FCSTD DOCUMENT  (FreeCAD 1.0R39109 (Git))
Label: 70_drawer_box_assembly
License: All rights reserved
LicenseURL: http://en.wikipedia.org/wiki/All_rights_reserved
objects: App::FeaturePython×25, App::Link×9, TechDraw::DrawViewDimension×7, TechDraw::DrawProjGroupItem×5, Assembly::JointGroup×2, Assembly::AssemblyObject×2, TechDraw::DrawSVGTemplate×1, TechDraw::DrawProjGroup×1, TechDraw::DrawPage×1
note: 13 computed .brp shape members not serialized (recipe doc carries the construction recipe); baked Part::Feature solids carry a one-line shape summary decoded from their .brp
EXTERNAL_REF file=71_drawer_box_top_bottom.FCStd obj=Body
EXTERNAL_REF file=73_drawer_box_side_b.FCStd obj=Body
EXTERNAL_REF file=72_drawer_box_side_a.FCStd obj=Body
EXTERNAL_REF file=junker_kv1-45-h45-l300-sc/kv1_h45_l350.FCStd obj=KV1_45_H45_L____SC
EXTERNAL_REF file=75_drawer_box_stabilizer.FCStd obj=Body

FEATURE [App::Link] Body
  LinkPlacement = pos=(0,0,0) rot=(0,0,1;3.14159rad)
  LinkedObject = -> <external 71_drawer_box_top_bottom.FCStd>#Body
  Placement = pos=(0,0,0) rot=(0,0,1;3.14159rad)
FEATURE [App::FeaturePython] GroundedJoint  # Assembly grounded joint (typed FeaturePython)
  ObjectToGround = -> Body
  Placement = pos=(0,0,0) rot=(0,0,1;3.14159rad)
FEATURE [App::Link] Body003
  LinkPlacement = pos=(2.045e-13,-6.16e-14,-771) rot=(1,0,0;3.14159rad)
  LinkedObject = -> <external 71_drawer_box_top_bottom.FCStd>#Body
  Placement = pos=(2.045e-13,-6.16e-14,-771) rot=(1,0,0;3.14159rad)
FEATURE [App::Link] Body004
  LinkPlacement = pos=(-262.5,7.5,-385.5) rot=(0,1,0;1.5708rad)
  LinkedObject = -> <external 73_drawer_box_side_b.FCStd>#Body
  Placement = pos=(-262.5,7.5,-385.5) rot=(0,1,0;1.5708rad)
FEATURE [App::Link] Body005
  LinkPlacement = pos=(244.5,7.5,-385.5) rot=(0,1,0;1.5708rad)
  LinkedObject = -> <external 72_drawer_box_side_a.FCStd>#Body
  Placement = pos=(244.5,7.5,-385.5) rot=(0,1,0;1.5708rad)
FEATURE [App::Link] KV1_45_H45_L____SC  label="KV1-45-H45-L...-SC"
  LinkPlacement = pos=(238.45,-31,-32) rot=(0,0.707107,-0.707107;3.14159rad)
  LinkedObject = -> <external junker_kv1-45-h45-l300-sc/kv1_h45_l350.FCStd>#KV1_45_H45_L____SC
  Placement = pos=(238.45,-31,-32) rot=(0,0.707107,-0.707107;3.14159rad)
FEATURE [TechDraw::DrawSVGTemplate] Template
  Height = 210
  Orientation = 1
  Template = C:/Program Files/FreeCAD 1.0/data/Mod/TechDraw/Templates/Default_Template_A4_Landscape.svg
  Width = 297
FEATURE [TechDraw::DrawProjGroupItem] View  label="Front"
  CoarseView = false
  Direction = (0,-1,0)
  Focus = 100
  HardHidden = false
  IsoCount = 0
  IsoHidden = false
  IsoVisible = false
  LockPosition = true
  Perspective = false
  Rotation = 0
  RotationVector = (1,0,0)
  Scale = 0.1
  ScaleType = 2
  ScrubCount = 1
  SeamHidden = false
  SeamVisible = true
  SmoothHidden = false
  SmoothVisible = true
  Type = 0
  X = 0
  XDirection = (1,0,0)
  XSource = -> [Body,Body003,Body004,Body005,KV1_45_H45_L____SC,Body007]
  Y = 0
FEATURE [TechDraw::DrawProjGroupItem] ProjItem  label="Right"
  CoarseView = false
  Direction = (1,-1e-16,0)
  Focus = 100
  HardHidden = false
  IsoCount = 0
  IsoHidden = false
  IsoVisible = false
  LockPosition = false
  Perspective = false
  Rotation = 0
  RotationVector = (1,0,0)
  ScaleType = 0
  ScrubCount = 1
  SeamHidden = false
  SeamVisible = true
  SmoothHidden = false
  SmoothVisible = true
  Type = 2
  X = -60.9
  XDirection = (1e-16,1,0)
  XSource = -> [Body,Body003,Body004,Body005,KV1_45_H45_L____SC,Body007]
  Y = 0
FEATURE [TechDraw::DrawProjGroupItem] ProjItem001  label="Bottom"
  CoarseView = false
  Direction = (0,0,-1)
  Focus = 100
  HardHidden = false
  IsoCount = 0
  IsoHidden = false
  IsoVisible = false
  LockPosition = false
  Perspective = false
  Rotation = 0
  RotationVector = (1,0,0)
  ScaleType = 0
  ScrubCount = 1
  SeamHidden = false
  SeamVisible = true
  SmoothHidden = false
  SmoothVisible = true
  Type = 5
  X = 0
  XDirection = (1,0,0)
  XSource = -> [Body,Body003,Body004,Body005,KV1_45_H45_L____SC,Body007]
  Y = 75
FEATURE [TechDraw::DrawProjGroupItem] ProjItem002  label="Left"
  CoarseView = false
  Direction = (-1,-1e-16,0)
  Focus = 100
  HardHidden = false
  IsoCount = 0
  IsoHidden = false
  IsoVisible = false
  LockPosition = false
  Perspective = false
  Rotation = 0
  RotationVector = (1,0,0)
  ScaleType = 0
  ScrubCount = 1
  SeamHidden = false
  SeamVisible = true
  SmoothHidden = false
  SmoothVisible = true
  Type = 1
  X = 60.9
  XDirection = (1e-16,-1,0)
  XSource = -> [Body,Body003,Body004,Body005,KV1_45_H45_L____SC,Body007]
  Y = 0
FEATURE [TechDraw::DrawProjGroupItem] ProjItem003  label="Top"
  CoarseView = false
  Direction = (0,0,1)
  Focus = 100
  HardHidden = false
  IsoCount = 0
  IsoHidden = false
  IsoVisible = false
  LockPosition = false
  Perspective = false
  Rotation = 0
  RotationVector = (1,0,0)
  ScaleType = 0
  ScrubCount = 1
  SeamHidden = false
  SeamVisible = true
  SmoothHidden = false
  SmoothVisible = true
  Type = 4
  X = 0
  XDirection = (1,0,0)
  XSource = -> [Body,Body003,Body004,Body005,KV1_45_H45_L____SC,Body007]
  Y = -75
FEATURE [TechDraw::DrawProjGroup] ProjGroup
  Anchor = -> View
  AutoDistribute = true
  LockPosition = false
  ProjectionType = 0
  Rotation = 0
  Scale = 0.1
  ScaleType = 2
  Views = -> [View,ProjItem,ProjItem001,ProjItem002,ProjItem003]
  X = 148.5
  XSource = -> [Body,Body003,Body004,Body005,KV1_45_H45_L____SC,Body007]
  Y = 105
  spacingX = 15
  spacingY = 15
FEATURE [TechDraw::DrawViewDimension] Dimension
  AngleOverride = false
  Arbitrary = false
  ArbitraryTolerances = false
  BoxCorners = (2) [(-26.25,-40.35,0),(26.25,40.35,0)]
  EqualTolerance = true
  ExtensionAngle = 0
  FormatSpec = %.2w
  FormatSpecOverTolerance = %+.2w
  FormatSpecUnderTolerance = %+.2w
  Inverted = false
  LineAngle = 0
  LockPosition = false
  MeasureType = 1
  OverTolerance = 0
  References2D = -> [View]
  Rotation = 0
  ScaleType = 0
  TheoreticalExact = false
  Type = 0
  UnderTolerance = 0
  X = 32.776
  Y = -39.775
FEATURE [TechDraw::DrawViewDimension] Dimension001
  AngleOverride = false
  Arbitrary = false
  ArbitraryTolerances = false
  BoxCorners = (2) [(-26.25,-40.35,0),(26.25,40.35,0)]
  EqualTolerance = true
  ExtensionAngle = 0
  FormatSpec = %.2w
  FormatSpecOverTolerance = %+.2w
  FormatSpecUnderTolerance = %+.2w
  Inverted = false
  LineAngle = 0
  LockPosition = false
  MeasureType = 1
  OverTolerance = 0
  References2D = -> [View]
  Rotation = 0
  ScaleType = 0
  TheoreticalExact = false
  Type = 0
  UnderTolerance = 0
  X = 32.776
  Y = 35.9189
FEATURE [TechDraw::DrawViewDimension] Dimension002
  AngleOverride = false
  Arbitrary = false
  ArbitraryTolerances = false
  BoxCorners = (2) [(-26.25,-40.35,0),(26.25,40.35,0)]
  EqualTolerance = true
  ExtensionAngle = 0
  FormatSpec = %.2w
  FormatSpecOverTolerance = %+.2w
  FormatSpecUnderTolerance = %+.2w
  Inverted = false
  LineAngle = 0
  LockPosition = false
  MeasureType = 1
  OverTolerance = 0
  References2D = -> [View]
  Rotation = 0
  ScaleType = 0
  TheoreticalExact = false
  Type = 0
  UnderTolerance = 0
  X = 36.8541
  Y = 21.3236
FEATURE [App::Link] Body007
  LinkPlacement = pos=(-2.61e-14,196.5,-386) rot=(0,-0.707107,0.707107;3.14159rad)
  LinkedObject = -> <external 75_drawer_box_stabilizer.FCStd>#Body
  Placement = pos=(-2.61e-14,196.5,-386) rot=(0,-0.707107,0.707107;3.14159rad)
FEATURE [App::FeaturePython] Joint  label="Distance"  # Assembly joint (typed FeaturePython)
  Activated = true
  AngleMax = 0
  AngleMin = 0
  Detach1 = false
  Detach2 = false
  Distance = 0
  Distance2 = 0
  EnableAngleMax = false
  EnableAngleMin = false
  EnableLengthMax = false
  EnableLengthMin = false
  JointType = 5 (Distance)
  LengthMax = 0
  LengthMin = 0
  Placement1 = pos=(-385.5,-1.21012,9.03703) rot=(-0.57735,-0.57735,0.57735;2.0944rad)
  Placement2 = pos=(5.5e-15,3.01501,0) rot=(0,0,1;0rad)
  Reference1 = -> Assembly [Body005.Face2,Body005.Vertex7]
  Reference2 = -> Assembly [Body.Face4,Body.Vertex10]
FEATURE [App::FeaturePython] Joint001  label="Distance001"  # Assembly joint (typed FeaturePython)
  Activated = true
  AngleMax = 0
  AngleMin = 0
  Detach1 = false
  Detach2 = false
  Distance = 0
  Distance2 = 0
  EnableAngleMax = false
  EnableAngleMin = false
  EnableLengthMax = false
  EnableLengthMin = false
  JointType = 5 (Distance)
  LengthMax = 0
  LengthMin = 0
  Placement1 = pos=(0,189,9) rot=(-1,0,0;1.5708rad)
  Placement2 = pos=(-5.9e-15,-196.5,9) rot=(0,0.707107,-0.707107;3.14159rad)
  Reference1 = -> Assembly [Body005.Face1,Body005.Vertex2]
  Reference2 = -> Assembly [Body.Face6,Body.Vertex6]
FEATURE [App::FeaturePython] Joint002  label="Distance002"  # Assembly joint (typed FeaturePython)
  Activated = true
  AngleMax = 0
  AngleMin = 0
  Detach1 = false
  Detach2 = false
  Distance = 0
  Distance2 = 0
  EnableAngleMax = false
  EnableAngleMin = false
  EnableLengthMax = false
  EnableLengthMin = false
  JointType = 5 (Distance)
  LengthMax = 0
  LengthMin = 0
  Placement1 = pos=(-262.5,-4.6e-15,9) rot=(-0.57735,-0.57735,0.57735;2.0944rad)
  Placement2 = pos=(0,3.6e-15,18) rot=(0,0,1;0rad)
  Reference1 = -> Assembly [Body.Face2,Body.Vertex6]
  Reference2 = -> Assembly [Body005.Face5,Body005.Vertex2]
FEATURE [App::FeaturePython] Joint003  label="Distance003"  # Assembly joint (typed FeaturePython)
  Activated = true
  AngleMax = 0
  AngleMin = 0
  Detach1 = false
  Detach2 = false
  Distance = 0
  Distance2 = 0
  EnableAngleMax = false
  EnableAngleMin = false
  EnableLengthMax = false
  EnableLengthMin = false
  JointType = 5 (Distance)
  LengthMax = 0
  LengthMin = 0
  Placement1 = pos=(-385.5,-1.21012,8.96297) rot=(-0.57735,-0.57735,0.57735;2.0944rad)
  Placement2 = pos=(5.5e-15,3.01501,0) rot=(0,0,1;0rad)
  Reference1 = -> Assembly [Body004.Face2,Body004.Face2]
  Reference2 = -> Assembly [Body.Face4,Body.Vertex3]
FEATURE [App::FeaturePython] Joint004  label="Distance004"  # Assembly joint (typed FeaturePython)
  Activated = true
  AngleMax = 0
  AngleMin = 0
  Detach1 = false
  Detach2 = false
  Distance = 0
  Distance2 = 0
  EnableAngleMax = false
  EnableAngleMin = false
  EnableLengthMax = false
  EnableLengthMin = false
  JointType = 5 (Distance)
  LengthMax = 0
  LengthMin = 0
  Placement1 = pos=(-5.9e-15,-196.5,9) rot=(0,0.707107,-0.707107;3.14159rad)
  Placement2 = pos=(0,189,9) rot=(-1,0,0;1.5708rad)
  Reference1 = -> Assembly [Body.Face6,Body.Vertex7]
  Reference2 = -> Assembly [Body004.Face1,Body004.Vertex1]
FEATURE [App::FeaturePython] Joint005  label="Distance005"  # Assembly joint (typed FeaturePython)
  Activated = true
  AngleMax = 0
  AngleMin = 0
  Detach1 = false
  Detach2 = false
  Distance = 0
  Distance2 = 0
  EnableAngleMax = false
  EnableAngleMin = false
  EnableLengthMax = false
  EnableLengthMin = false
  JointType = 5 (Distance)
  LengthMax = 0
  LengthMin = 0
  Placement1 = pos=(262.5,4.6e-15,9) rot=(-0.57735,0.57735,-0.57735;2.0944rad)
  Placement2 = pos=(0,7.1e-15,0) rot=(0,0,1;0rad)
  Reference1 = -> Assembly [Body.Face3,Body.Vertex8]
  Reference2 = -> Assembly [Body004.Face4,Body004.Vertex1]
FEATURE [App::FeaturePython] Joint006  label="Distance006"  # Assembly joint (typed FeaturePython)
  Activated = true
  AngleMax = 0
  AngleMin = 0
  Detach1 = false
  Detach2 = false
  Distance = 0
  Distance2 = 0
  EnableAngleMax = false
  EnableAngleMin = false
  EnableLengthMax = false
  EnableLengthMin = false
  JointType = 5 (Distance)
  LengthMax = 0
  LengthMin = 0
  Placement1 = pos=(-262.5,-6.4e-15,9) rot=(-0.57735,-0.57735,0.57735;2.0944rad)
  Placement2 = pos=(0,7.1e-15,0) rot=(0,0,1;0rad)
  Reference1 = -> Assembly [Body003.Face2,Body003.Vertex1]
  Reference2 = -> Assembly [Body004.Face4,Body004.Vertex3]
FEATURE [App::FeaturePython] Joint007  label="Distance007"  # Assembly joint (typed FeaturePython)
  Activated = true
  AngleMax = 0
  AngleMin = 0
  Detach1 = false
  Detach2 = false
  Distance = 0
  Distance2 = 0
  EnableAngleMax = false
  EnableAngleMin = false
  EnableLengthMax = false
  EnableLengthMin = false
  JointType = 5 (Distance)
  LengthMax = 0
  LengthMin = 0
  Placement1 = pos=(4.7e-15,3.01501,0) rot=(0,0,1;0rad)
  Placement2 = pos=(385.5,-1.21012,8.96297) rot=(-0.57735,0.57735,-0.57735;2.0944rad)
  Reference1 = -> Assembly [Body003.Face4,Body003.Vertex1]
  Reference2 = -> Assembly [Body004.Face3,Body004.Vertex13]
FEATURE [App::FeaturePython] Joint008  label="Distance008"  # Assembly joint (typed FeaturePython)
  Activated = true
  AngleMax = 0
  AngleMin = 0
  Detach1 = false
  Detach2 = false
  Distance = 0
  Distance2 = 0
  EnableAngleMax = false
  EnableAngleMin = false
  EnableLengthMax = false
  EnableLengthMin = false
  JointType = 5 (Distance)
  LengthMax = 0
  LengthMin = 0
  Placement1 = pos=(-2e-16,-196.5,9) rot=(0,0.707107,-0.707107;3.14159rad)
  Placement2 = pos=(0,189,9) rot=(-1,0,0;1.5708rad)
  Reference1 = -> Assembly [Body003.Face6,Body003.Vertex5]
  Reference2 = -> Assembly [Body004.Face1,Body004.Vertex4]
FEATURE [App::FeaturePython] Joint009  label="Distance009"  # Assembly joint (typed FeaturePython)
  Activated = true
  AngleMax = 0
  AngleMin = 0
  Detach1 = false
  Detach2 = false
  Distance = 0
  Distance2 = 0
  EnableAngleMax = false
  EnableAngleMin = false
  EnableLengthMax = false
  EnableLengthMin = false
  JointType = 5 (Distance)
  LengthMax = 0
  LengthMin = 0
  Placement1 = pos=(-244.5,7.39e-13,8.98683) rot=(0.57735,0.57735,-0.57735;4.18879rad)
  Placement2 = pos=(0.0538161,-6.11853,0) rot=(0,0,1;0rad)
  Reference1 = -> Assembly [Body007.Face5,Body007.Face5]
  Reference2 = -> Assembly [Body005.Face6,Body005.Vertex47]
FEATURE [App::FeaturePython] Joint010  label="Distance010"  # Assembly joint (typed FeaturePython)
  Activated = true
  AngleMax = 0
  AngleMin = 0
  Detach1 = false
  Detach2 = false
  Distance = 0
  Distance2 = 0
  EnableAngleMax = false
  EnableAngleMin = false
  EnableLengthMax = false
  EnableLengthMin = false
  JointType = 5 (Distance)
  LengthMax = 0
  LengthMin = 0
  Placement1 = pos=(-1.29e-14,0,0) rot=(0,0,1;0rad)
  Placement2 = pos=(0,189,9) rot=(-1,0,0;1.5708rad)
  Reference1 = -> Assembly [Body007.Face2,Body007.Face2]
  Reference2 = -> Assembly [Body004.Face1,Body004.Face1]
FEATURE [App::FeaturePython] Joint011  label="Distance011"  # Assembly joint (typed FeaturePython)
  Activated = true
  AngleMax = 0
  AngleMin = 0
  Detach1 = false
  Detach2 = false
  Distance = 335.5
  Distance2 = 0
  EnableAngleMax = false
  EnableAngleMin = false
  EnableLengthMax = false
  EnableLengthMin = false
  JointType = 5 (Distance)
  LengthMax = 0
  LengthMin = 0
  Placement1 = pos=(-8.8e-15,-50.5,3) rot=(0,0.707107,-0.707107;3.14159rad)
  Placement2 = pos=(5.5e-15,3.01501,0) rot=(0,0,1;0rad)
  Reference1 = -> Assembly [Body007.Face6,Body007.Face6]
  Reference2 = -> Assembly [Body.Face4,Body.Vertex10]
  expr: Distance = (771 - 100) / 2
FEATURE [App::FeaturePython] Joint012  label="Distance012"  # Assembly joint (typed FeaturePython)
  Activated = true
  AngleMax = 0
  AngleMin = 0
  Detach1 = false
  Detach2 = false
  Distance = 0
  Distance2 = 0
  EnableAngleMax = false
  EnableAngleMin = false
  EnableLengthMax = false
  EnableLengthMin = false
  JointType = 5 (Distance)
  LengthMax = 0
  LengthMin = 0
  Placement1 = pos=(-1.2,0.000268538,-180.383) rot=(-0.57735,-0.57735,0.57735;2.0944rad)
  Placement2 = pos=(0.0538161,-6.11853,0) rot=(0,0,1;0rad)
  Reference1 = -> Assembly [KV1_45_H45_L____SC.Junker_H45SC_op_350.Part__Feature.Face126,KV1_45_H45_L____SC.Junker_H45SC_op_350.Part__Feature.Vertex163]
  Reference2 = -> Assembly [Body005.Face6,Body005.Vertex6]
FEATURE [App::FeaturePython] Joint013  label="Distance013"  # Assembly joint (typed FeaturePython)
  Activated = true
  AngleMax = 0
  AngleMin = 0
  Detach1 = false
  Detach2 = false
  Distance = -0.5
  Distance2 = 0
  EnableAngleMax = false
  EnableAngleMin = false
  EnableLengthMax = false
  EnableLengthMin = false
  JointType = 5 (Distance)
  LengthMax = 0
  LengthMin = 0
  Placement1 = pos=(0,-189,9) rot=(0,-0.707107,0.707107;3.14159rad)
  Placement2 = pos=(1.78975,1.17e-14,0) rot=(0,0,1;0rad)
  Reference1 = -> Assembly [Body005.Face10,Body005.Face10]
  Reference2 = -> Assembly [KV1_45_H45_L____SC.Junker_H45SC_op_350.Part__Feature.Face145,KV1_45_H45_L____SC.Junker_H45SC_op_350.Part__Feature.Face145]
FEATURE [App::FeaturePython] Joint014  label="Cylindrical"  # Assembly joint (typed FeaturePython)
  Activated = true
  AngleMax = 0
  AngleMin = 0
  Detach1 = false
  Detach2 = false
  Distance = 0
  Distance2 = 0
  EnableAngleMax = false
  EnableAngleMin = false
  EnableLengthMax = false
  EnableLengthMin = false
  JointType = 2 (Cylindrical)
  LengthMax = 0
  LengthMin = 0
  Placement1 = pos=(-353.5,-81,4.5) rot=(0,0,1;0rad)
  Placement2 = pos=(-0.6,0,-107.5) rot=(0,1,0;1.5708rad)
  Reference1 = -> Assembly [Body005.Face11,Body005.Face11]
  Reference2 = -> Assembly [KV1_45_H45_L____SC.Junker_H45SC_op_350.Part__Feature.Face31,KV1_45_H45_L____SC.Junker_H45SC_op_350.Part__Feature.Face31]
FEATURE [Assembly::JointGroup] Joints001
FEATURE [Assembly::AssemblyObject] Assembly001
  Group = -> [Joints001]
  Origin = -> Origin001
  Type = Assembly
FEATURE [App::Link] KV1_45_H45_L____SC001  label="KV1-45-H45-L...-SC001"
  LinkPlacement = pos=(238.45,-31,-224) rot=(0,0.707107,-0.707107;3.14159rad)
  LinkedObject = -> <external junker_kv1-45-h45-l300-sc/kv1_h45_l350.FCStd>#KV1_45_H45_L____SC
  Placement = pos=(238.45,-31,-224) rot=(0,0.707107,-0.707107;3.14159rad)
FEATURE [App::Link] KV1_45_H45_L____SC002  label="KV1-45-H45-L...-SC002"
  LinkPlacement = pos=(238.45,-31,-128) rot=(0,0.707107,-0.707107;3.14159rad)
  LinkedObject = -> <external junker_kv1-45-h45-l300-sc/kv1_h45_l350.FCStd>#KV1_45_H45_L____SC
  Placement = pos=(238.45,-31,-128) rot=(0,0.707107,-0.707107;3.14159rad)
FEATURE [App::Link] KV1_45_H45_L____SC003  label="KV1-45-H45-L...-SC003"
  LinkPlacement = pos=(238.45,-31,-320) rot=(0,0.707107,-0.707107;3.14159rad)
  LinkedObject = -> <external junker_kv1-45-h45-l300-sc/kv1_h45_l350.FCStd>#KV1_45_H45_L____SC
  Placement = pos=(238.45,-31,-320) rot=(0,0.707107,-0.707107;3.14159rad)
FEATURE [App::FeaturePython] Joint015  label="Distance014"  # Assembly joint (typed FeaturePython)
  Activated = true
  AngleMax = 0
  AngleMin = 0
  Detach1 = false
  Detach2 = false
  Distance = 0
  Distance2 = 0
  EnableAngleMax = false
  EnableAngleMin = false
  EnableLengthMax = false
  EnableLengthMin = false
  JointType = 5 (Distance)
  LengthMax = 0
  LengthMin = 0
  Placement1 = pos=(-1.2,0.000268538,-180.383) rot=(-0.57735,-0.57735,0.57735;2.0944rad)
  Placement2 = pos=(0.0538161,-6.11853,0) rot=(0,0,1;0rad)
  Reference1 = -> Assembly [KV1_45_H45_L____SC002.Junker_H45SC_op_350.Part__Feature.Face126,KV1_45_H45_L____SC002.Junker_H45SC_op_350.Part__Feature.Vertex163]
  Reference2 = -> Assembly [Body005.Face6,Body005.Vertex23]
FEATURE [App::FeaturePython] Joint016  label="Distance015"  # Assembly joint (typed FeaturePython)
  Activated = true
  AngleMax = 0
  AngleMin = 0
  Detach1 = false
  Detach2 = false
  Distance = -0.5
  Distance2 = 0
  EnableAngleMax = false
  EnableAngleMin = false
  EnableLengthMax = false
  EnableLengthMin = false
  JointType = 5 (Distance)
  LengthMax = 0
  LengthMin = 0
  Placement1 = pos=(0,-189,9) rot=(0,-0.707107,0.707107;3.14159rad)
  Placement2 = pos=(1.78975,1.17e-14,0) rot=(0,0,1;0rad)
  Reference1 = -> Assembly [Body005.Face10,Body005.Vertex5]
  Reference2 = -> Assembly [KV1_45_H45_L____SC002.Junker_H45SC_op_350.Part__Feature.Face145,KV1_45_H45_L____SC002.Junker_H45SC_op_350.Part__Feature.Face145]
FEATURE [App::FeaturePython] Joint017  label="Distance016"  # Assembly joint (typed FeaturePython)
  Activated = true
  AngleMax = 0
  AngleMin = 0
  Detach1 = false
  Detach2 = false
  Distance = 0
  Distance2 = 0
  EnableAngleMax = false
  EnableAngleMin = false
  EnableLengthMax = false
  EnableLengthMin = false
  JointType = 5 (Distance)
  LengthMax = 0
  LengthMin = 0
  Placement1 = pos=(-1.2,0.000268538,-180.383) rot=(-0.57735,-0.57735,0.57735;2.0944rad)
  Placement2 = pos=(0.0538161,-6.11853,0) rot=(0,0,1;0rad)
  Reference1 = -> Assembly [KV1_45_H45_L____SC003.Junker_H45SC_op_350.Part__Feature.Face126,KV1_45_H45_L____SC003.Junker_H45SC_op_350.Part__Feature.Vertex171]
  Reference2 = -> Assembly [Body005.Face6,Body005.Vertex21]
FEATURE [App::FeaturePython] Joint018  label="Distance017"  # Assembly joint (typed FeaturePython)
  Activated = true
  AngleMax = 0
  AngleMin = 0
  Detach1 = false
  Detach2 = false
  Distance = 0.5
  Distance2 = 0
  EnableAngleMax = false
  EnableAngleMin = false
  EnableLengthMax = false
  EnableLengthMin = false
  JointType = 5 (Distance)
  LengthMax = 0
  LengthMin = 0
  Placement1 = pos=(1.78975,1.17e-14,0) rot=(0,0,1;0rad)
  Placement2 = pos=(0,-189,9) rot=(0,-0.707107,0.707107;3.14159rad)
  Reference1 = -> Assembly [KV1_45_H45_L____SC003.Junker_H45SC_op_350.Part__Feature.Face145,KV1_45_H45_L____SC003.Junker_H45SC_op_350.Part__Feature.Vertex242]
  Reference2 = -> Assembly [Body005.Face10,Body005.Face10]
FEATURE [App::FeaturePython] Joint019  label="Distance018"  # Assembly joint (typed FeaturePython)
  Activated = true
  AngleMax = 0
  AngleMin = 0
  Detach1 = false
  Detach2 = false
  Distance = 0
  Distance2 = 0
  EnableAngleMax = false
  EnableAngleMin = false
  EnableLengthMax = false
  EnableLengthMin = false
  JointType = 5 (Distance)
  LengthMax = 0
  LengthMin = 0
  Placement1 = pos=(-1.2,0.000268538,-180.383) rot=(-0.57735,-0.57735,0.57735;2.0944rad)
  Placement2 = pos=(0.0538161,-6.11853,0) rot=(0,0,1;0rad)
  Reference1 = -> Assembly [KV1_45_H45_L____SC001.Junker_H45SC_op_350.Part__Feature.Face126,KV1_45_H45_L____SC001.Junker_H45SC_op_350.Part__Feature.Edge73]
  Reference2 = -> Assembly [Body005.Face6,Body005.Vertex21]
FEATURE [App::FeaturePython] Joint020  label="Distance019"  # Assembly joint (typed FeaturePython)
  Activated = true
  AngleMax = 0
  AngleMin = 0
  Detach1 = false
  Detach2 = false
  Distance = -0.5
  Distance2 = 0
  EnableAngleMax = false
  EnableAngleMin = false
  EnableLengthMax = false
  EnableLengthMin = false
  JointType = 5 (Distance)
  LengthMax = 0
  LengthMin = 0
  Placement1 = pos=(0,-189,9) rot=(0,-0.707107,0.707107;3.14159rad)
  Placement2 = pos=(-1.2,0,0) rot=(-0.57735,-0.57735,0.57735;4.18879rad)
  Reference1 = -> Assembly [Body005.Face10,Body005.Face10]
  Reference2 = -> Assembly [KV1_45_H45_L____SC001.Junker_H45SC_op_350.Part__Feature.Edge368,KV1_45_H45_L____SC001.Junker_H45SC_op_350.Part__Feature.Vertex242]
FEATURE [App::FeaturePython] Joint021  label="Cylindrical001"  # Assembly joint (typed FeaturePython)
  Activated = true
  AngleMax = 0
  AngleMin = 0
  Detach1 = false
  Detach2 = false
  Distance = 0
  Distance2 = 0
  EnableAngleMax = false
  EnableAngleMin = false
  EnableLengthMax = false
  EnableLengthMin = false
  JointType = 2 (Cylindrical)
  LengthMax = 0
  LengthMin = 0
  Placement1 = pos=(-0.6,0,-107.5) rot=(0,1,0;1.5708rad)
  Placement2 = pos=(-257.5,-81,0) rot=(0,0,1;0rad)
  Reference1 = -> Assembly [KV1_45_H45_L____SC002.Junker_H45SC_op_350.Part__Feature.Face31,KV1_45_H45_L____SC002.Junker_H45SC_op_350.Part__Feature.Face31]
  Reference2 = -> Assembly [Body005.Face14,Body005.Edge3]
FEATURE [App::FeaturePython] Joint022  label="Cylindrical002"  # Assembly joint (typed FeaturePython)
  Activated = true
  AngleMax = 0
  AngleMin = 0
  Detach1 = false
  Detach2 = false
  Distance = 0
  Distance2 = 0
  EnableAngleMax = false
  EnableAngleMin = false
  EnableLengthMax = false
  EnableLengthMin = false
  JointType = 2 (Cylindrical)
  LengthMax = 0
  LengthMin = 0
  Placement1 = pos=(-161.5,-81,0) rot=(0,0,1;0rad)
  Placement2 = pos=(-0.6,0,-107.5) rot=(0,1,0;1.5708rad)
  Reference1 = -> Assembly [Body005.Face17,Body005.Edge3]
  Reference2 = -> Assembly [KV1_45_H45_L____SC001.Junker_H45SC_op_350.Part__Feature.Face31,KV1_45_H45_L____SC001.Junker_H45SC_op_350.Part__Feature.Face31]
FEATURE [App::FeaturePython] Joint023  label="Cylindrical003"  # Assembly joint (typed FeaturePython)
  Activated = true
  AngleMax = 0
  AngleMin = 0
  Detach1 = false
  Detach2 = false
  Distance = 0
  Distance2 = 0
  EnableAngleMax = false
  EnableAngleMin = false
  EnableLengthMax = false
  EnableLengthMin = false
  JointType = 2 (Cylindrical)
  LengthMax = 0
  LengthMin = 0
  Placement1 = pos=(-65.5,-81,0) rot=(0,0,1;0rad)
  Placement2 = pos=(-0.6,0,-107.5) rot=(0,1,0;1.5708rad)
  Reference1 = -> Assembly [Body005.Face20,Body005.Edge3]
  Reference2 = -> Assembly [KV1_45_H45_L____SC003.Junker_H45SC_op_350.Part__Feature.Face31,KV1_45_H45_L____SC003.Junker_H45SC_op_350.Part__Feature.Face31]
FEATURE [Assembly::JointGroup] Joints
  Group = -> [GroundedJoint,Joint,Joint001,Joint002,Joint003,Joint004,Joint005,Joint006,Joint007,Joint008,Joint009,Joint010,Joint011,Joint012,Joint013,Joint014,Joint015,Joint016,Joint017,Joint018,Joint019,Joint020,Joint021,Joint022,Joint023]
FEATURE [Assembly::AssemblyObject] Assembly
  Group = -> [Joints,Body,GroundedJoint,Body003,Body004,Body005,KV1_45_H45_L____SC,Body007,Joint,Joint001,Joint002,Joint003,Joint004,Joint005,Joint006,Joint007,Joint008,Joint009,Joint010,Joint011,Joint012,Joint013,Joint014,Assembly001,KV1_45_H45_L____SC001,KV1_45_H45_L____SC002,KV1_45_H45_L____SC003,Joint015,Joint016,Joint017,Joint018,Joint019,Joint020,Joint021,Joint022,Joint023]
  Origin = -> Origin
  Type = Assembly
FEATURE [TechDraw::DrawViewDimension] Dimension003
  AngleOverride = false
  Arbitrary = false
  ArbitraryTolerances = false
  BoxCorners = (2) [(-26.25,-40.35,-1e-07),(26.25,40.35,1e-07)]
  EqualTolerance = true
  ExtensionAngle = 0
  FormatSpec = %.2w
  FormatSpecOverTolerance = %+.2w
  FormatSpecUnderTolerance = %+.2w
  Inverted = false
  LineAngle = 0
  LockPosition = false
  MeasureType = 1
  OverTolerance = 0
  References2D = -> [View]
  Rotation = 0
  ScaleType = 0
  TheoreticalExact = false
  Type = 0
  UnderTolerance = 0
  X = 27.7175
  Y = -21.8
FEATURE [TechDraw::DrawViewDimension] Dimension004
  AngleOverride = false
  Arbitrary = false
  ArbitraryTolerances = false
  BoxCorners = (2) [(-26.25,-40.35,-1e-07),(26.25,40.35,1e-07)]
  EqualTolerance = true
  ExtensionAngle = 0
  FormatSpec = %.2w
  FormatSpecOverTolerance = %+.2w
  FormatSpecUnderTolerance = %+.2w
  Inverted = false
  LineAngle = 0
  LockPosition = false
  MeasureType = 1
  OverTolerance = 0
  References2D = -> [View]
  Rotation = 0
  ScaleType = 0
  TheoreticalExact = false
  Type = 1
  UnderTolerance = 0
  X = 0
  Y = -22.7337
FEATURE [TechDraw::DrawViewDimension] Dimension005
  AngleOverride = false
  Arbitrary = false
  ArbitraryTolerances = false
  BoxCorners = (2) [(-26.25,-40.35,-1e-07),(26.25,40.35,1e-07)]
  EqualTolerance = true
  ExtensionAngle = 0
  FormatSpec = %.2w
  FormatSpecOverTolerance = %+.2w
  FormatSpecUnderTolerance = %+.2w
  Inverted = false
  LineAngle = 0
  LockPosition = false
  MeasureType = 1
  OverTolerance = 0
  References2D = -> [View]
  Rotation = 0
  ScaleType = 0
  TheoreticalExact = false
  Type = 0
  UnderTolerance = 0
  X = 32.776
  Y = 7.8134
FEATURE [TechDraw::DrawViewDimension] Dimension006
  AngleOverride = false
  Arbitrary = false
  ArbitraryTolerances = false
  BoxCorners = (2) [(-19.65,-40.35,0),(19.65,40.35,0)]
  EqualTolerance = true
  ExtensionAngle = 0
  FormatSpec = %.2w
  FormatSpecOverTolerance = %+.2w
  FormatSpecUnderTolerance = %+.2w
  Inverted = false
  LineAngle = 0
  LockPosition = false
  MeasureType = 1
  OverTolerance = 0
  References2D = -> [ProjItem]
  Rotation = 0
  ScaleType = 0
  TheoreticalExact = false
  Type = 0
  UnderTolerance = 0
  X = 4.61091
  Y = -56.391
FEATURE [TechDraw::DrawPage] Page
  KeepUpdated = true
  NextBalloonIndex = 1
  ProjectionType = 0
  Template = -> Template
  Views = -> [ProjGroup,Dimension,Dimension001,Dimension002,Dimension003,Dimension004,Dimension005,Dimension006]

RESOLVED EXTERNAL PARTS (link-assembly join: the EXTERNAL_REF files above that resolve inside this repo's crawl, each included once):
---- part 71_drawer_box_top_bottom.FCStd = doc fcstd_6746109f4d4a ----
FCSTD DOCUMENT  (FreeCAD 1.0R39109 (Git))
Label: 71_drawer_box_top_bottom
License: All rights reserved
LicenseURL: http://en.wikipedia.org/wiki/All_rights_reserved
objects: Sketcher::SketchObject×2, Spreadsheet::Sheet×1, PartDesign::Pad×1, PartDesign::Pocket×1, PartDesign::Body×1
note: 11 computed .brp shape members not serialized (recipe doc carries the construction recipe); baked Part::Feature solids carry a one-line shape summary decoded from their .brp

FEATURE [Spreadsheet::Sheet] Spreadsheet
  cells = A2='length; B2(length)=525; A3='width; B3(width)=393; A4='height; B4(height)=18
FEATURE [Sketcher::SketchObject] Sketch
  ArcFitTolerance = 0
  AttachmentSupport = -> [XY_Plane]
  FullyConstrained = true
  MakeInternals = false
  MapMode = 5
  expr: Constraints[11] = Spreadsheet.length
  expr: Constraints[12] = Spreadsheet.width
  sketch-geometry (5):
    g0: LineSegment StartX=-262.5 StartY=196.5 StartZ=0 EndX=262.5 EndY=196.5 EndZ=0
    g1: LineSegment StartX=262.5 StartY=196.5 StartZ=0 EndX=262.5 EndY=-196.5 EndZ=0
    g2: LineSegment StartX=262.5 StartY=-196.5 StartZ=0 EndX=-262.5 EndY=-196.5 EndZ=0
    g3: LineSegment StartX=-262.5 StartY=-196.5 StartZ=0 EndX=-262.5 EndY=196.5 EndZ=0
    g4: LineSegment [constr] StartX=-262.5 StartY=196.5 StartZ=0 EndX=262.5 EndY=-196.5 EndZ=0
  constraints (13):
    c: Coincident(g0,g1)
    c: Coincident(g1,g2)
    c: Coincident(g2,g3)
    c: Coincident(g3,g0)
    c: Horizontal(g0)
    c: Horizontal(g2)
    c: Vertical(g1)
    c: Vertical(g3)
    c: Coincident(g4,g1)
    c: Coincident(g0,g4)
    c: Symmetric(g0,g1,g-1)
    c: Distance(g0,g0) = 525
    c: Distance(g0,g2) = 393
FEATURE [PartDesign::Pad] Pad
  Direction = (0,0,1)
  Length = 18
  Length2 = 10
  Profile = -> Sketch
  ReferenceAxis = -> Sketch [N_Axis]
  Suppressed = false
  Type = 0
  expr: Length = Spreadsheet.height
FEATURE [Sketcher::SketchObject] Sketch001
  ArcFitTolerance = 1e-06
  AttachmentSupport = -> [YZ_Plane]
  ExternalGeometry = -> [Pad]
  FullyConstrained = true
  MakeInternals = false
  MapMode = 5
  Placement = pos=(0,0,0) rot=(0.57735,0.57735,0.57735;2.0944rad)
  sketch-geometry (4):
    g0: LineSegment StartX=-190.5 StartY=0 StartZ=0 EndX=-184 EndY=0 EndZ=0
    g1: LineSegment StartX=-184 StartY=0 StartZ=0 EndX=-184 EndY=7 EndZ=0
    g2: LineSegment StartX=-184 StartY=7 StartZ=0 EndX=-190.5 EndY=7 EndZ=0
    g3: LineSegment StartX=-190.5 StartY=7 StartZ=0 EndX=-190.5 EndY=0 EndZ=0
  constraints (12):
    c: Coincident(g0,g1)
    c: Coincident(g1,g2)
    c: Coincident(g2,g3)
    c: Coincident(g3,g0)
    c: Horizontal(g0)
    c: Horizontal(g2)
    c: Vertical(g1)
    c: Vertical(g3)
    c: PointOnObject(g0,g-5)
    c: DistanceX(g2,g2) = 6.5
    c: DistanceY(g3,g3) = 7
    c: Distance(g3,g-4) = 6
FEATURE [PartDesign::Pocket] Pocket
  BaseFeature = -> Pad
  Direction = (-1,0,0)
  Length = 251.5
  Length2 = 251.5
  Profile = -> Sketch001
  ReferenceAxis = -> Sketch001 [N_Axis]
  Suppressed = false
  Type = 4
  expr: Length = Spreadsheet.length / 2 - 11
  expr: Length2 = Spreadsheet.length / 2 - 11
FEATURE [PartDesign::Body] Body
  AllowCompound = false
  Group = -> [Sketch,Pad,Sketch001,Pocket]
  Origin = -> Origin
  Tip = -> Pocket
---- part 72_drawer_box_side_a.FCStd = doc fcstd_383eb0427cff ----
FCSTD DOCUMENT  (FreeCAD 1.0R39109 (Git))
Label: 72_drawer_box_side_a
License: All rights reserved
LicenseURL: http://en.wikipedia.org/wiki/All_rights_reserved
objects: Sketcher::SketchObject×3, PartDesign::Pocket×2, Spreadsheet::Sheet×1, PartDesign::Pad×1, PartDesign::Body×1
note: 16 computed .brp shape members not serialized (recipe doc carries the construction recipe); baked Part::Feature solids carry a one-line shape summary decoded from their .brp

FEATURE [Spreadsheet::Sheet] Spreadsheet
  cells = A2='length; B2(length)=771; A3='width; B3(width)=378; A4='height; B4(height)=18; A5='euro32Distance; B5(euro32Distance)=32; A6='euro32Holedia; B6(euro32Holedia)=5
FEATURE [Sketcher::SketchObject] Sketch
  ArcFitTolerance = 0
  AttachmentSupport = -> [XY_Plane]
  FullyConstrained = true
  MakeInternals = false
  MapMode = 5
  expr: Constraints[11] = Spreadsheet.length
  expr: Constraints[12] = Spreadsheet.width
  sketch-geometry (5):
    g0: LineSegment StartX=-385.5 StartY=189 StartZ=0 EndX=385.5 EndY=189 EndZ=0
    g1: LineSegment StartX=385.5 StartY=189 StartZ=0 EndX=385.5 EndY=-189 EndZ=0
    g2: LineSegment StartX=385.5 StartY=-189 StartZ=0 EndX=-385.5 EndY=-189 EndZ=0
    g3: LineSegment StartX=-385.5 StartY=-189 StartZ=0 EndX=-385.5 EndY=189 EndZ=0
    g4: LineSegment [constr] StartX=-385.5 StartY=189 StartZ=0 EndX=385.5 EndY=-189 EndZ=0
  constraints (13):
    c: Coincident(g0,g1)
    c: Coincident(g1,g2)
    c: Coincident(g2,g3)
    c: Coincident(g3,g0)
    c: Horizontal(g0)
    c: Horizontal(g2)
    c: Vertical(g1)
    c: Vertical(g3)
    c: Coincident(g4,g1)
    c: Coincident(g0,g4)
    c: Symmetric(g0,g1,g-1)
    c: Distance(g0,g0) = 771
    c: Distance(g0,g2) = 378
FEATURE [PartDesign::Pad] Pad
  Direction = (0,0,1)
  Length = 18
  Length2 = 10
  Profile = -> Sketch
  ReferenceAxis = -> Sketch [N_Axis]
  Suppressed = false
  Type = 0
  expr: Length = Spreadsheet.height
FEATURE [Sketcher::SketchObject] Sketch001
  ArcFitTolerance = 1e-06
  AttachmentOffset = pos=(0,0,9) rot=(0,0,1;0rad)
  AttachmentSupport = -> [XY_Plane]
  ExternalGeometry = -> [Pad]
  FullyConstrained = true
  MakeInternals = false
  MapMode = 5
  Placement = pos=(0,0,9) rot=(0,0,1;0rad)
  expr: Constraints[102] = Spreadsheet.euro32Distance
  expr: Constraints[103] = Spreadsheet.euro32Distance
  expr: Constraints[104] = Spreadsheet.euro32Distance
  expr: Constraints[105] = Spreadsheet.euro32Distance
  expr: Constraints[106] = Spreadsheet.euro32Distance
  expr: Constraints[107] = Spreadsheet.euro32Distance
  expr: Constraints[108] = Spreadsheet.euro32Distance
  expr: Constraints[109] = Spreadsheet.euro32Distance
  expr: Constraints[10] = Spreadsheet.euro32Holedia
  expr: Constraints[110] = Spreadsheet.euro32Distance
  expr: Constraints[111] = Spreadsheet.euro32Distance
  expr: Constraints[112] = 32 mm
  expr: Constraints[113] = Spreadsheet.euro32Distance
  expr: Constraints[114] = Spreadsheet.euro32Distance
  expr: Constraints[115] = Spreadsheet.euro32Distance
  expr: Constraints[116] = Spreadsheet.euro32Distance
  expr: Constraints[117] = Spreadsheet.euro32Distance
  expr: Constraints[118] = Spreadsheet.euro32Distance
  expr: Constraints[119] = Spreadsheet.euro32Distance
  expr: Constraints[11] = Spreadsheet.euro32Holedia
  expr: Constraints[120] = Spreadsheet.euro32Distance
  expr: Constraints[12] = Spreadsheet.euro32Holedia
  expr: Constraints[13] = Spreadsheet.euro32Holedia
  expr: Constraints[14] = Spreadsheet.euro32Holedia
  expr: Constraints[15] = Spreadsheet.euro32Holedia
  expr: Constraints[16] = Spreadsheet.euro32Holedia
  expr: Constraints[17] = Spreadsheet.euro32Holedia
  expr: Constraints[18] = Spreadsheet.euro32Holedia
  expr: Constraints[19] = Spreadsheet.euro32Holedia
  expr: Constraints[22] = Spreadsheet.euro32Distance
  expr: Constraints[23] = Spreadsheet.euro32Holedia
  expr: Constraints[24] = Spreadsheet.euro32Distance
  expr: Constraints[44] = Spreadsheet.euro32Holedia
  expr: Constraints[45] = Spreadsheet.euro32Holedia
  expr: Constraints[46] = Spreadsheet.euro32Holedia
  expr: Constraints[47] = Spreadsheet.euro32Holedia
  expr: Constraints[48] = Spreadsheet.euro32Holedia
  expr: Constraints[49] = Spreadsheet.euro32Holedia
  expr: Constraints[4] = Spreadsheet.euro32Holedia
  expr: Constraints[50] = Spreadsheet.euro32Distance
  expr: Constraints[51] = Spreadsheet.euro32Distance
  expr: Constraints[52] = Spreadsheet.euro32Distance
  expr: Constraints[53] = Spreadsheet.euro32Distance
  expr: Constraints[54] = Spreadsheet.euro32Distance
  expr: Constraints[55] = Spreadsheet.euro32Distance
  expr: Constraints[56] = Spreadsheet.euro32Distance
  expr: Constraints[57] = Spreadsheet.euro32Distance
  expr: Constraints[58] = Spreadsheet.euro32Distance
  expr: Constraints[59] = Spreadsheet.euro32Distance
  expr: Constraints[60] = Spreadsheet.euro32Distance
  expr: Constraints[61] = Spreadsheet.euro32Distance
  expr: Constraints[62] = Spreadsheet.euro32Distance
  expr: Constraints[63] = Spreadsheet.euro32Distance
  expr: Constraints[64] = Spreadsheet.euro32Distance
  expr: Constraints[65] = Spreadsheet.euro32Distance
  expr: Constraints[66] = Spreadsheet.euro32Distance
  expr: Constraints[67] = Spreadsheet.euro32Distance
  expr: Constraints[68] = Spreadsheet.euro32Distance
  expr: Constraints[6] = Spreadsheet.euro32Holedia
  expr: Constraints[75] = Spreadsheet.euro32Holedia
  expr: Constraints[7] = Spreadsheet.euro32Holedia
  expr: Constraints[80] = Spreadsheet.euro32Distance
  expr: Constraints[81] = Spreadsheet.euro32Distance
  expr: Constraints[8] = Spreadsheet.euro32Holedia
  expr: Constraints[9] = Spreadsheet.euro32Holedia
  sketch-geometry (46):
    g0: LineSegment [constr] StartX=-385.5 StartY=-81 StartZ=0 EndX=385.5 EndY=-81 EndZ=0
    g1: Circle CenterX=-376 CenterY=-81 CenterZ=0 NormalX=0 NormalY=0 NormalZ=1 AngleXU=0 Radius=2.5
    g2: Circle CenterX=-344 CenterY=-81 CenterZ=0 NormalX=0 NormalY=0 NormalZ=1 AngleXU=0 Radius=2.5
    g3: Circle CenterX=-312 CenterY=-81 CenterZ=0 NormalX=0 NormalY=0 NormalZ=1 AngleXU=0 Radius=2.5
    g4: Circle CenterX=-280 CenterY=-81 CenterZ=0 NormalX=0 NormalY=0 NormalZ=1 AngleXU=0 Radius=2.5
    g5: Circle CenterX=-248 CenterY=-81 CenterZ=0 NormalX=0 NormalY=0 NormalZ=1 AngleXU=0 Radius=2.5
    g6: Circle CenterX=-216 CenterY=-81 CenterZ=0 NormalX=0 NormalY=0 NormalZ=1 AngleXU=0 Radius=2.5
    g7: Circle CenterX=-184 CenterY=-81 CenterZ=0 NormalX=0 NormalY=0 NormalZ=1 AngleXU=0 Radius=2.5
    g8: Circle CenterX=-152 CenterY=-81 CenterZ=0 NormalX=0 NormalY=0 NormalZ=1 AngleXU=0 Radius=2.5
    g9: Circle CenterX=-120 CenterY=-81 CenterZ=0 NormalX=0 NormalY=0 NormalZ=1 AngleXU=0 Radius=2.5
    g10: Circle CenterX=-88 CenterY=-81 CenterZ=0 NormalX=0 NormalY=0 NormalZ=1 AngleXU=0 Radius=2.5
    g11: Circle CenterX=-56 CenterY=-81 CenterZ=0 NormalX=0 NormalY=0 NormalZ=1 AngleXU=0 Radius=2.5
    g12: Circle CenterX=-24 CenterY=-81 CenterZ=0 NormalX=0 NormalY=0 NormalZ=1 AngleXU=0 Radius=2.5
    g13: Circle CenterX=8 CenterY=-81 CenterZ=0 NormalX=0 NormalY=0 NormalZ=1 AngleXU=0 Radius=2.5
    g14: Circle CenterX=40 CenterY=-81 CenterZ=0 NormalX=0 NormalY=0 NormalZ=1 AngleXU=0 Radius=2.5
    g15: Circle CenterX=72 CenterY=-81 CenterZ=0 NormalX=0 NormalY=0 NormalZ=1 AngleXU=0 Radius=2.5
    g16: Circle CenterX=104 CenterY=-81 CenterZ=0 NormalX=0 NormalY=0 NormalZ=1 AngleXU=0 Radius=2.5
    g17: Circle CenterX=136 CenterY=-81 CenterZ=0 NormalX=0 NormalY=0 NormalZ=1 AngleXU=0 Radius=2.5
    g18: Circle CenterX=168 CenterY=-81 CenterZ=0 NormalX=0 NormalY=0 NormalZ=1 AngleXU=0 Radius=2.5
    g19: Circle CenterX=200 CenterY=-81 CenterZ=0 NormalX=0 NormalY=0 NormalZ=1 AngleXU=0 Radius=2.5
    g20: Circle CenterX=232 CenterY=-81 CenterZ=0 NormalX=0 NormalY=0 NormalZ=1 AngleXU=0 Radius=2.5
    g21: Circle CenterX=264 CenterY=-81 CenterZ=0 NormalX=0 NormalY=0 NormalZ=1 AngleXU=0 Radius=2.5
    g22: Circle CenterX=296 CenterY=-81 CenterZ=0 NormalX=0 NormalY=0 NormalZ=1 AngleXU=0 Radius=2.5
    g23: LineSegment [constr] StartX=-385.5 StartY=-17 StartZ=0 EndX=385.5 EndY=-17 EndZ=0
    g24: Circle CenterX=-376 CenterY=-17 CenterZ=0 NormalX=0 NormalY=0 NormalZ=1 AngleXU=0 Radius=2.5
    g25: Circle CenterX=-344 CenterY=-17 CenterZ=0 NormalX=0 NormalY=0 NormalZ=1 AngleXU=0 Radius=2.5
    g26: Circle CenterX=-312 CenterY=-17 CenterZ=0 NormalX=0 NormalY=0 NormalZ=1 AngleXU=0 Radius=2.5
    g27: Circle CenterX=-280 CenterY=-17 CenterZ=0 NormalX=0 NormalY=0 NormalZ=1 AngleXU=0 Radius=2.5
    g28: Circle CenterX=-248 CenterY=-17 CenterZ=0 NormalX=0 NormalY=0 NormalZ=1 AngleXU=0 Radius=2.5
    g29: Circle CenterX=-216 CenterY=-17 CenterZ=0 NormalX=0 NormalY=0 NormalZ=1 AngleXU=0 Radius=2.5
    g30: Circle CenterX=-184 CenterY=-17 CenterZ=0 NormalX=0 NormalY=0 NormalZ=1 AngleXU=0 Radius=2.5
    g31: Circle CenterX=-152 CenterY=-17 CenterZ=0 NormalX=0 NormalY=0 NormalZ=1 AngleXU=0 Radius=2.5
    g32: Circle CenterX=-120 CenterY=-17 CenterZ=0 NormalX=0 NormalY=0 NormalZ=1 AngleXU=0 Radius=2.5
    g33: Circle CenterX=-88 CenterY=-17 CenterZ=0 NormalX=0 NormalY=0 NormalZ=1 AngleXU=0 Radius=2.5
    g34: Circle CenterX=-56 CenterY=-17 CenterZ=0 NormalX=0 NormalY=0 NormalZ=1 AngleXU=0 Radius=2.5
    g35: Circle CenterX=-24 CenterY=-17 CenterZ=0 NormalX=0 NormalY=0 NormalZ=1 AngleXU=0 Radius=2.5
    g36: Circle CenterX=8 CenterY=-17 CenterZ=0 NormalX=0 NormalY=0 NormalZ=1 AngleXU=0 Radius=2.5
    g37: Circle CenterX=40 CenterY=-17 CenterZ=0 NormalX=0 NormalY=0 NormalZ=1 AngleXU=0 Radius=2.5
    g38: Circle CenterX=72 CenterY=-17 CenterZ=0 NormalX=0 NormalY=0 NormalZ=1 AngleXU=0 Radius=2.5
    g39: Circle CenterX=104 CenterY=-17 CenterZ=0 NormalX=0 NormalY=0 NormalZ=1 AngleXU=0 Radius=2.5
    g40: Circle CenterX=136 CenterY=-17 CenterZ=0 NormalX=0 NormalY=0 NormalZ=1 AngleXU=0 Radius=2.5
    g41: Circle CenterX=168 CenterY=-17 CenterZ=0 NormalX=0 NormalY=0 NormalZ=1 AngleXU=0 Radius=2.5
    g42: Circle CenterX=200 CenterY=-17 CenterZ=0 NormalX=0 NormalY=0 NormalZ=1 AngleXU=0 Radius=2.5
    g43: Circle CenterX=232 CenterY=-17 CenterZ=0 NormalX=0 NormalY=0 NormalZ=1 AngleXU=0 Radius=2.5
    g44: Circle CenterX=264 CenterY=-17 CenterZ=0 NormalX=0 NormalY=0 NormalZ=1 AngleXU=0 Radius=2.5
    g45: Circle CenterX=296 CenterY=-17 CenterZ=0 NormalX=0 NormalY=0 NormalZ=1 AngleXU=0 Radius=2.5
  constraints (140):
    c: PointOnObject(g0,g-3)
    c: PointOnObject(g0,g-4)
    c: Horizontal(g0)
    c: PointOnObject(g1,g0)
    c: Diameter(g1) = 5
    c: Distance(g1,g-3) = 9.5
    c: Diameter(g9) = 5
    c: Diameter(g10) = 5
    c: Diameter(g11) = 5
    c: Diameter(g12) = 5
    c: Diameter(g13) = 5
    c: Diameter(g14) = 5
    c: Diameter(g15) = 5
    c: Diameter(g16) = 5
    c: Diameter(g17) = 5
    c: Diameter(g18) = 5
    c: Diameter(g19) = 5
    c: Diameter(g20) = 5
    c: Diameter(g21) = 5
    c: Diameter(g22) = 5
    c: PointOnObject(g2,g0)
    c: PointOnObject(g3,g0)
    c: DistanceX(g1,g2) = 32
    c: Diameter(g2) = 5
    c: DistanceX(g2,g3) = 32
    c: PointOnObject(g4,g0)
    c: PointOnObject(g5,g0)
    c: PointOnObject(g6,g0)
    c: PointOnObject(g7,g0)
    c: PointOnObject(g8,g0)
    c: PointOnObject(g9,g0)
    c: PointOnObject(g10,g0)
    c: PointOnObject(g11,g0)
    c: PointOnObject(g12,g0)
    c: PointOnObject(g13,g0)
    c: PointOnObject(g14,g0)
    c: PointOnObject(g15,g0)
    c: PointOnObject(g16,g0)
    c: PointOnObject(g17,g0)
    c: PointOnObject(g18,g0)
    c: PointOnObject(g19,g0)
    c: PointOnObject(g20,g0)
    c: PointOnObject(g21,g0)
    c: PointOnObject(g22,g0)
    c: Diameter(g8) = 5
    c: Diameter(g7) = 5
    c: Diameter(g6) = 5
    c: Diameter(g5) = 5
    c: Diameter(g4) = 5
    c: Diameter(g3) = 5
    c: DistanceX(g3,g4) = 32
    c: DistanceX(g4,g5) = 32
    c: DistanceX(g5,g6) = 32
    c: DistanceX(g6,g7) = 32
    c: DistanceX(g7,g8) = 32
    c: DistanceX(g8,g9) = 32
    c: DistanceX(g9,g10) = 32
    c: DistanceX(g10,g11) = 32
    c: DistanceX(g11,g12) = 32
    c: DistanceX(g12,g13) = 32
    c: DistanceX(g13,g14) = 32
    c: DistanceX(g14,g15) = 32
    c: DistanceX(g15,g16) = 32
    c: DistanceX(g16,g17) = 32
    c: DistanceX(g17,g18) = 32
    c: DistanceX(g18,g19) = 32
    c: DistanceX(g19,g20) = 32
    c: DistanceX(g20,g21) = 32
    c: DistanceX(g21,g22) = 32
    c: DistanceY(g-3,g0) = 108
    c: PointOnObject(g23,g-3)
    c: PointOnObject(g23,g-4)
    c: Horizontal(g23)
    c: Distance(g0,g23) = 64
    c: PointOnObject(g24,g23)
    c: Diameter(g24) = 5
    c: Equal(g24,g25)
    c: Equal(g24,g26)
    c: PointOnObject(g25,g23)
    c: PointOnObject(g26,g23)
    c: Distance(g24,g25) = 32
    c: DistanceX(g25,g26) = 32
    c: Distance(g24,g-3) = 9.5
    c: Equal(g27,g24)
    c: Equal(g28,g24)
    c: Equal(g29,g24)
    c: Equal(g30,g24)
    c: Equal(g31,g24)
    c: Equal(g32,g24)
    c: Equal(g33,g24)
    c: Equal(g34,g24)
    c: Equal(g35,g24)
    c: Equal(g36,g24)
    c: Equal(g37,g24)
    c: Equal(g38,g24)
    c: Equal(g39,g24)
    c: Equal(g40,g24)
    c: Equal(g41,g24)
    c: Equal(g42,g24)
    c: Equal(g43,g24)
    c: Equal(g44,g24)
    c: Equal(g45,g24)
    c: Distance(g26,g27) = 32
    c: DistanceX(g27,g28) = 32
    c: Distance(g28,g29) = 32
    c: Distance(g29,g30) = 32
    c: Distance(g30,g31) = 32
    c: Distance(g31,g32) = 32
    c: Distance(g32,g33) = 32
    c: Distance(g33,g34) = 32
    c: Distance(g34,g35) = 32
    c: Distance(g35,g36) = 32
    c: Distance(g36,g37) = 32
    c: DistanceX(g37,g38) = 32
    c: DistanceX(g38,g39) = 32
    c: Distance(g39,g40) = 32
    c: Distance(g40,g41) = 32
    c: Distance(g42,g41) = 32
    c: Distance(g43,g42) = 32
    c: Distance(g44,g43) = 32
    c: DistanceX(g44,g45) = 32
    c: PointOnObject(g27,g23)
    c: PointOnObject(g28,g23)
    c: PointOnObject(g29,g23)
    c: PointOnObject(g30,g23)
    c: PointOnObject(g31,g23)
    c: PointOnObject(g32,g23)
    c: PointOnObject(g33,g23)
    c: PointOnObject(g34,g23)
    c: PointOnObject(g35,g23)
    c: PointOnObject(g36,g23)
    c: PointOnObject(g37,g23)
    c: PointOnObject(g38,g23)
    c: PointOnObject(g39,g23)
    c: PointOnObject(g40,g23)
    c: PointOnObject(g41,g23)
    c: PointOnObject(g42,g23)
    c: PointOnObject(g43,g23)
    c: PointOnObject(g44,g23)
    c: PointOnObject(g45,g23)
FEATURE [PartDesign::Pocket] Pocket
  BaseFeature = -> Pad
  Direction = (0,0,-1)
  Length = 9
  Length2 = 5
  Profile = -> Sketch001
  ReferenceAxis = -> Sketch001 [N_Axis]
  Suppressed = false
  Type = 0
FEATURE [Sketcher::SketchObject] Sketch002
  ArcFitTolerance = 1e-06
  AttachmentSupport = -> [YZ_Plane]
  ExternalGeometry = -> [Pocket]
  FullyConstrained = true
  MakeInternals = false
  MapMode = 5
  Placement = pos=(0,0,0) rot=(0.57735,0.57735,0.57735;2.0944rad)
  sketch-geometry (4):
    g0: LineSegment StartX=176.5 StartY=0 StartZ=0 EndX=183 EndY=0 EndZ=0
    g1: LineSegment StartX=183 StartY=0 StartZ=0 EndX=183 EndY=7 EndZ=0
    g2: LineSegment StartX=183 StartY=7 StartZ=0 EndX=176.5 EndY=7 EndZ=0
    g3: LineSegment StartX=176.5 StartY=7 StartZ=0 EndX=176.5 EndY=0 EndZ=0
  constraints (12):
    c: Coincident(g0,g1)
    c: Coincident(g1,g2)
    c: Coincident(g2,g3)
    c: Coincident(g3,g0)
    c: Horizontal(g0)
    c: Horizontal(g2)
    c: Vertical(g1)
    c: Vertical(g3)
    c: PointOnObject(g0,g-5)
    c: Distance(g-3,g1) = 6
    c: DistanceY(g3,g3) = 7
    c: DistanceX(g2,g2) = 6.5
FEATURE [PartDesign::Pocket] Pocket001
  BaseFeature = -> Pocket
  Direction = (-1,0,0)
  Length = 550
  Length2 = 550
  Profile = -> Sketch002
  ReferenceAxis = -> Sketch002 [N_Axis]
  Suppressed = false
  Type = 4
FEATURE [PartDesign::Body] Body
  AllowCompound = false
  Group = -> [Sketch,Pad,Sketch001,Pocket,Sketch002,Pocket001]
  Origin = -> Origin
  Tip = -> Pocket001
---- part 73_drawer_box_side_b.FCStd = doc fcstd_3bf29c370427 ----
FCSTD DOCUMENT  (FreeCAD 1.0R39109 (Git))
Label: 73_drawer_box_side_b
License: All rights reserved
LicenseURL: http://en.wikipedia.org/wiki/All_rights_reserved
objects: Sketcher::SketchObject×3, PartDesign::Pocket×2, Spreadsheet::Sheet×1, PartDesign::Pad×1, PartDesign::Body×1
note: 16 computed .brp shape members not serialized (recipe doc carries the construction recipe); baked Part::Feature solids carry a one-line shape summary decoded from their .brp

FEATURE [Spreadsheet::Sheet] Spreadsheet
  cells = A2='length; B2(length)=771; A3='width; B3(width)=378; A4='height; B4(height)=18; A5='euro32Distance; B5(euro32Distance)=32; A6='euro32Holedia; B6(euro32Holedia)=5
FEATURE [Sketcher::SketchObject] Sketch
  ArcFitTolerance = 0
  AttachmentSupport = -> [XY_Plane]
  FullyConstrained = true
  MakeInternals = false
  MapMode = 5
  expr: Constraints[11] = Spreadsheet.length
  expr: Constraints[12] = Spreadsheet.width
  sketch-geometry (5):
    g0: LineSegment StartX=-385.5 StartY=189 StartZ=0 EndX=385.5 EndY=189 EndZ=0
    g1: LineSegment StartX=385.5 StartY=189 StartZ=0 EndX=385.5 EndY=-189 EndZ=0
    g2: LineSegment StartX=385.5 StartY=-189 StartZ=0 EndX=-385.5 EndY=-189 EndZ=0
    g3: LineSegment StartX=-385.5 StartY=-189 StartZ=0 EndX=-385.5 EndY=189 EndZ=0
    g4: LineSegment [constr] StartX=-385.5 StartY=189 StartZ=0 EndX=385.5 EndY=-189 EndZ=0
  constraints (13):
    c: Coincident(g0,g1)
    c: Coincident(g1,g2)
    c: Coincident(g2,g3)
    c: Coincident(g3,g0)
    c: Horizontal(g0)
    c: Horizontal(g2)
    c: Vertical(g1)
    c: Vertical(g3)
    c: Coincident(g4,g1)
    c: Coincident(g0,g4)
    c: Symmetric(g0,g1,g-1)
    c: Distance(g0,g0) = 771
    c: Distance(g0,g2) = 378
FEATURE [PartDesign::Pad] Pad
  Direction = (0,0,1)
  Length = 18
  Length2 = 10
  Profile = -> Sketch
  ReferenceAxis = -> Sketch [N_Axis]
  Suppressed = false
  Type = 0
  expr: Length = Spreadsheet.height
FEATURE [Sketcher::SketchObject] Sketch001
  ArcFitTolerance = 1e-06
  AttachmentOffset = pos=(0,0,9) rot=(0,0,1;0rad)
  AttachmentSupport = -> [XY_Plane]
  ExternalGeometry = -> [Pad]
  FullyConstrained = true
  MakeInternals = false
  MapMode = 5
  Placement = pos=(0,0,9) rot=(0,0,1;0rad)
  expr: Constraints[102] = Spreadsheet.euro32Distance
  expr: Constraints[103] = Spreadsheet.euro32Distance
  expr: Constraints[104] = Spreadsheet.euro32Distance
  expr: Constraints[105] = Spreadsheet.euro32Distance
  expr: Constraints[106] = Spreadsheet.euro32Distance
  expr: Constraints[107] = Spreadsheet.euro32Distance
  expr: Constraints[108] = Spreadsheet.euro32Distance
  expr: Constraints[109] = Spreadsheet.euro32Distance
  expr: Constraints[10] = Spreadsheet.euro32Holedia
  expr: Constraints[110] = Spreadsheet.euro32Distance
  expr: Constraints[111] = Spreadsheet.euro32Distance
  expr: Constraints[112] = 32 mm
  expr: Constraints[113] = Spreadsheet.euro32Distance
  expr: Constraints[114] = Spreadsheet.euro32Distance
  expr: Constraints[115] = Spreadsheet.euro32Distance
  expr: Constraints[116] = Spreadsheet.euro32Distance
  expr: Constraints[117] = Spreadsheet.euro32Distance
  expr: Constraints[118] = Spreadsheet.euro32Distance
  expr: Constraints[119] = Spreadsheet.euro32Distance
  expr: Constraints[11] = Spreadsheet.euro32Holedia
  expr: Constraints[120] = Spreadsheet.euro32Distance
  expr: Constraints[12] = Spreadsheet.euro32Holedia
  expr: Constraints[13] = Spreadsheet.euro32Holedia
  expr: Constraints[14] = Spreadsheet.euro32Holedia
  expr: Constraints[15] = Spreadsheet.euro32Holedia
  expr: Constraints[16] = Spreadsheet.euro32Holedia
  expr: Constraints[17] = Spreadsheet.euro32Holedia
  expr: Constraints[18] = Spreadsheet.euro32Holedia
  expr: Constraints[19] = Spreadsheet.euro32Holedia
  expr: Constraints[22] = Spreadsheet.euro32Distance
  expr: Constraints[23] = Spreadsheet.euro32Holedia
  expr: Constraints[24] = Spreadsheet.euro32Distance
  expr: Constraints[44] = Spreadsheet.euro32Holedia
  expr: Constraints[45] = Spreadsheet.euro32Holedia
  expr: Constraints[46] = Spreadsheet.euro32Holedia
  expr: Constraints[47] = Spreadsheet.euro32Holedia
  expr: Constraints[48] = Spreadsheet.euro32Holedia
  expr: Constraints[49] = Spreadsheet.euro32Holedia
  expr: Constraints[4] = Spreadsheet.euro32Holedia
  expr: Constraints[50] = Spreadsheet.euro32Distance
  expr: Constraints[51] = Spreadsheet.euro32Distance
  expr: Constraints[52] = Spreadsheet.euro32Distance
  expr: Constraints[53] = Spreadsheet.euro32Distance
  expr: Constraints[54] = Spreadsheet.euro32Distance
  expr: Constraints[55] = Spreadsheet.euro32Distance
  expr: Constraints[56] = Spreadsheet.euro32Distance
  expr: Constraints[57] = Spreadsheet.euro32Distance
  expr: Constraints[58] = Spreadsheet.euro32Distance
  expr: Constraints[59] = Spreadsheet.euro32Distance
  expr: Constraints[60] = Spreadsheet.euro32Distance
  expr: Constraints[61] = Spreadsheet.euro32Distance
  expr: Constraints[62] = Spreadsheet.euro32Distance
  expr: Constraints[63] = Spreadsheet.euro32Distance
  expr: Constraints[64] = Spreadsheet.euro32Distance
  expr: Constraints[65] = Spreadsheet.euro32Distance
  expr: Constraints[66] = Spreadsheet.euro32Distance
  expr: Constraints[67] = Spreadsheet.euro32Distance
  expr: Constraints[68] = Spreadsheet.euro32Distance
  expr: Constraints[6] = Spreadsheet.euro32Holedia
  expr: Constraints[75] = Spreadsheet.euro32Holedia
  expr: Constraints[7] = Spreadsheet.euro32Holedia
  expr: Constraints[80] = Spreadsheet.euro32Distance
  expr: Constraints[81] = Spreadsheet.euro32Distance
  expr: Constraints[8] = Spreadsheet.euro32Holedia
  expr: Constraints[9] = Spreadsheet.euro32Holedia
  sketch-geometry (46):
    g0: LineSegment [constr] StartX=-385.5 StartY=-81 StartZ=0 EndX=385.5 EndY=-81 EndZ=0
    g1: Circle CenterX=-376 CenterY=-81 CenterZ=0 NormalX=0 NormalY=0 NormalZ=1 AngleXU=0 Radius=2.5
    g2: Circle CenterX=-344 CenterY=-81 CenterZ=0 NormalX=0 NormalY=0 NormalZ=1 AngleXU=0 Radius=2.5
    g3: Circle CenterX=-312 CenterY=-81 CenterZ=0 NormalX=0 NormalY=0 NormalZ=1 AngleXU=0 Radius=2.5
    g4: Circle CenterX=-280 CenterY=-81 CenterZ=0 NormalX=0 NormalY=0 NormalZ=1 AngleXU=0 Radius=2.5
    g5: Circle CenterX=-248 CenterY=-81 CenterZ=0 NormalX=0 NormalY=0 NormalZ=1 AngleXU=0 Radius=2.5
    g6: Circle CenterX=-216 CenterY=-81 CenterZ=0 NormalX=0 NormalY=0 NormalZ=1 AngleXU=0 Radius=2.5
    g7: Circle CenterX=-184 CenterY=-81 CenterZ=0 NormalX=0 NormalY=0 NormalZ=1 AngleXU=0 Radius=2.5
    g8: Circle CenterX=-152 CenterY=-81 CenterZ=0 NormalX=0 NormalY=0 NormalZ=1 AngleXU=0 Radius=2.5
    g9: Circle CenterX=-120 CenterY=-81 CenterZ=0 NormalX=0 NormalY=0 NormalZ=1 AngleXU=0 Radius=2.5
    g10: Circle CenterX=-88 CenterY=-81 CenterZ=0 NormalX=0 NormalY=0 NormalZ=1 AngleXU=0 Radius=2.5
    g11: Circle CenterX=-56 CenterY=-81 CenterZ=0 NormalX=0 NormalY=0 NormalZ=1 AngleXU=0 Radius=2.5
    g12: Circle CenterX=-24 CenterY=-81 CenterZ=0 NormalX=0 NormalY=0 NormalZ=1 AngleXU=0 Radius=2.5
    g13: Circle CenterX=8 CenterY=-81 CenterZ=0 NormalX=0 NormalY=0 NormalZ=1 AngleXU=0 Radius=2.5
    g14: Circle CenterX=40 CenterY=-81 CenterZ=0 NormalX=0 NormalY=0 NormalZ=1 AngleXU=0 Radius=2.5
    g15: Circle CenterX=72 CenterY=-81 CenterZ=0 NormalX=0 NormalY=0 NormalZ=1 AngleXU=0 Radius=2.5
    g16: Circle CenterX=104 CenterY=-81 CenterZ=0 NormalX=0 NormalY=0 NormalZ=1 AngleXU=0 Radius=2.5
    g17: Circle CenterX=136 CenterY=-81 CenterZ=0 NormalX=0 NormalY=0 NormalZ=1 AngleXU=0 Radius=2.5
    g18: Circle CenterX=168 CenterY=-81 CenterZ=0 NormalX=0 NormalY=0 NormalZ=1 AngleXU=0 Radius=2.5
    g19: Circle CenterX=200 CenterY=-81 CenterZ=0 NormalX=0 NormalY=0 NormalZ=1 AngleXU=0 Radius=2.5
    g20: Circle CenterX=232 CenterY=-81 CenterZ=0 NormalX=0 NormalY=0 NormalZ=1 AngleXU=0 Radius=2.5
    g21: Circle CenterX=264 CenterY=-81 CenterZ=0 NormalX=0 NormalY=0 NormalZ=1 AngleXU=0 Radius=2.5
    g22: Circle CenterX=296 CenterY=-81 CenterZ=0 NormalX=0 NormalY=0 NormalZ=1 AngleXU=0 Radius=2.5
    g23: LineSegment [constr] StartX=-385.5 StartY=-17 StartZ=0 EndX=385.5 EndY=-17 EndZ=0
    g24: Circle CenterX=-376 CenterY=-17 CenterZ=0 NormalX=0 NormalY=0 NormalZ=1 AngleXU=0 Radius=2.5
    g25: Circle CenterX=-344 CenterY=-17 CenterZ=0 NormalX=0 NormalY=0 NormalZ=1 AngleXU=0 Radius=2.5
    g26: Circle CenterX=-312 CenterY=-17 CenterZ=0 NormalX=0 NormalY=0 NormalZ=1 AngleXU=0 Radius=2.5
    g27: Circle CenterX=-280 CenterY=-17 CenterZ=0 NormalX=0 NormalY=0 NormalZ=1 AngleXU=0 Radius=2.5
    g28: Circle CenterX=-248 CenterY=-17 CenterZ=0 NormalX=0 NormalY=0 NormalZ=1 AngleXU=0 Radius=2.5
    g29: Circle CenterX=-216 CenterY=-17 CenterZ=0 NormalX=0 NormalY=0 NormalZ=1 AngleXU=0 Radius=2.5
    g30: Circle CenterX=-184 CenterY=-17 CenterZ=0 NormalX=0 NormalY=0 NormalZ=1 AngleXU=0 Radius=2.5
    g31: Circle CenterX=-152 CenterY=-17 CenterZ=0 NormalX=0 NormalY=0 NormalZ=1 AngleXU=0 Radius=2.5
    g32: Circle CenterX=-120 CenterY=-17 CenterZ=0 NormalX=0 NormalY=0 NormalZ=1 AngleXU=0 Radius=2.5
    g33: Circle CenterX=-88 CenterY=-17 CenterZ=0 NormalX=0 NormalY=0 NormalZ=1 AngleXU=0 Radius=2.5
    g34: Circle CenterX=-56 CenterY=-17 CenterZ=0 NormalX=0 NormalY=0 NormalZ=1 AngleXU=0 Radius=2.5
    g35: Circle CenterX=-24 CenterY=-17 CenterZ=0 NormalX=0 NormalY=0 NormalZ=1 AngleXU=0 Radius=2.5
    g36: Circle CenterX=8 CenterY=-17 CenterZ=0 NormalX=0 NormalY=0 NormalZ=1 AngleXU=0 Radius=2.5
    g37: Circle CenterX=40 CenterY=-17 CenterZ=0 NormalX=0 NormalY=0 NormalZ=1 AngleXU=0 Radius=2.5
    g38: Circle CenterX=72 CenterY=-17 CenterZ=0 NormalX=0 NormalY=0 NormalZ=1 AngleXU=0 Radius=2.5
    g39: Circle CenterX=104 CenterY=-17 CenterZ=0 NormalX=0 NormalY=0 NormalZ=1 AngleXU=0 Radius=2.5
    g40: Circle CenterX=136 CenterY=-17 CenterZ=0 NormalX=0 NormalY=0 NormalZ=1 AngleXU=0 Radius=2.5
    g41: Circle CenterX=168 CenterY=-17 CenterZ=0 NormalX=0 NormalY=0 NormalZ=1 AngleXU=0 Radius=2.5
    g42: Circle CenterX=200 CenterY=-17 CenterZ=0 NormalX=0 NormalY=0 NormalZ=1 AngleXU=0 Radius=2.5
    g43: Circle CenterX=232 CenterY=-17 CenterZ=0 NormalX=0 NormalY=0 NormalZ=1 AngleXU=0 Radius=2.5
    g44: Circle CenterX=264 CenterY=-17 CenterZ=0 NormalX=0 NormalY=0 NormalZ=1 AngleXU=0 Radius=2.5
    g45: Circle CenterX=296 CenterY=-17 CenterZ=0 NormalX=0 NormalY=0 NormalZ=1 AngleXU=0 Radius=2.5
  constraints (140):
    c: PointOnObject(g0,g-3)
    c: PointOnObject(g0,g-4)
    c: Horizontal(g0)
    c: PointOnObject(g1,g0)
    c: Diameter(g1) = 5
    c: Distance(g1,g-3) = 9.5
    c: Diameter(g9) = 5
    c: Diameter(g10) = 5
    c: Diameter(g11) = 5
    c: Diameter(g12) = 5
    c: Diameter(g13) = 5
    c: Diameter(g14) = 5
    c: Diameter(g15) = 5
    c: Diameter(g16) = 5
    c: Diameter(g17) = 5
    c: Diameter(g18) = 5
    c: Diameter(g19) = 5
    c: Diameter(g20) = 5
    c: Diameter(g21) = 5
    c: Diameter(g22) = 5
    c: PointOnObject(g2,g0)
    c: PointOnObject(g3,g0)
    c: DistanceX(g1,g2) = 32
    c: Diameter(g2) = 5
    c: DistanceX(g2,g3) = 32
    c: PointOnObject(g4,g0)
    c: PointOnObject(g5,g0)
    c: PointOnObject(g6,g0)
    c: PointOnObject(g7,g0)
    c: PointOnObject(g8,g0)
    c: PointOnObject(g9,g0)
    c: PointOnObject(g10,g0)
    c: PointOnObject(g11,g0)
    c: PointOnObject(g12,g0)
    c: PointOnObject(g13,g0)
    c: PointOnObject(g14,g0)
    c: PointOnObject(g15,g0)
    c: PointOnObject(g16,g0)
    c: PointOnObject(g17,g0)
    c: PointOnObject(g18,g0)
    c: PointOnObject(g19,g0)
    c: PointOnObject(g20,g0)
    c: PointOnObject(g21,g0)
    c: PointOnObject(g22,g0)
    c: Diameter(g8) = 5
    c: Diameter(g7) = 5
    c: Diameter(g6) = 5
    c: Diameter(g5) = 5
    c: Diameter(g4) = 5
    c: Diameter(g3) = 5
    c: DistanceX(g3,g4) = 32
    c: DistanceX(g4,g5) = 32
    c: DistanceX(g5,g6) = 32
    c: DistanceX(g6,g7) = 32
    c: DistanceX(g7,g8) = 32
    c: DistanceX(g8,g9) = 32
    c: DistanceX(g9,g10) = 32
    c: DistanceX(g10,g11) = 32
    c: DistanceX(g11,g12) = 32
    c: DistanceX(g12,g13) = 32
    c: DistanceX(g13,g14) = 32
    c: DistanceX(g14,g15) = 32
    c: DistanceX(g15,g16) = 32
    c: DistanceX(g16,g17) = 32
    c: DistanceX(g17,g18) = 32
    c: DistanceX(g18,g19) = 32
    c: DistanceX(g19,g20) = 32
    c: DistanceX(g20,g21) = 32
    c: DistanceX(g21,g22) = 32
    c: DistanceY(g-3,g0) = 108
    c: PointOnObject(g23,g-3)
    c: PointOnObject(g23,g-4)
    c: Horizontal(g23)
    c: Distance(g0,g23) = 64
    c: PointOnObject(g24,g23)
    c: Diameter(g24) = 5
    c: Equal(g24,g25)
    c: Equal(g24,g26)
    c: PointOnObject(g25,g23)
    c: PointOnObject(g26,g23)
    c: Distance(g24,g25) = 32
    c: DistanceX(g25,g26) = 32
    c: Distance(g24,g-3) = 9.5
    c: Equal(g27,g24)
    c: Equal(g28,g24)
    c: Equal(g29,g24)
    c: Equal(g30,g24)
    c: Equal(g31,g24)
    c: Equal(g32,g24)
    c: Equal(g33,g24)
    c: Equal(g34,g24)
    c: Equal(g35,g24)
    c: Equal(g36,g24)
    c: Equal(g37,g24)
    c: Equal(g38,g24)
    c: Equal(g39,g24)
    c: Equal(g40,g24)
    c: Equal(g41,g24)
    c: Equal(g42,g24)
    c: Equal(g43,g24)
    c: Equal(g44,g24)
    c: Equal(g45,g24)
    c: Distance(g26,g27) = 32
    c: DistanceX(g27,g28) = 32
    c: Distance(g28,g29) = 32
    c: Distance(g29,g30) = 32
    c: Distance(g30,g31) = 32
    c: Distance(g31,g32) = 32
    c: Distance(g32,g33) = 32
    c: Distance(g33,g34) = 32
    c: Distance(g34,g35) = 32
    c: Distance(g35,g36) = 32
    c: Distance(g36,g37) = 32
    c: DistanceX(g37,g38) = 32
    c: DistanceX(g38,g39) = 32
    c: Distance(g39,g40) = 32
    c: Distance(g40,g41) = 32
    c: Distance(g42,g41) = 32
    c: Distance(g43,g42) = 32
    c: Distance(g44,g43) = 32
    c: DistanceX(g44,g45) = 32
    c: PointOnObject(g27,g23)
    c: PointOnObject(g28,g23)
    c: PointOnObject(g29,g23)
    c: PointOnObject(g30,g23)
    c: PointOnObject(g31,g23)
    c: PointOnObject(g32,g23)
    c: PointOnObject(g33,g23)
    c: PointOnObject(g34,g23)
    c: PointOnObject(g35,g23)
    c: PointOnObject(g36,g23)
    c: PointOnObject(g37,g23)
    c: PointOnObject(g38,g23)
    c: PointOnObject(g39,g23)
    c: PointOnObject(g40,g23)
    c: PointOnObject(g41,g23)
    c: PointOnObject(g42,g23)
    c: PointOnObject(g43,g23)
    c: PointOnObject(g44,g23)
    c: PointOnObject(g45,g23)
FEATURE [PartDesign::Pocket] Pocket
  BaseFeature = -> Pad
  Direction = (0,0,-1)
  Length = 9
  Length2 = 5
  Profile = -> Sketch001
  ReferenceAxis = -> Sketch001 [N_Axis]
  Reversed = true
  Suppressed = false
  Type = 0
FEATURE [Sketcher::SketchObject] Sketch003
  ArcFitTolerance = 1e-06
  AttachmentSupport = -> [YZ_Plane]
  ExternalGeometry = -> [Pocket]
  FullyConstrained = true
  MakeInternals = false
  MapMode = 5
  Placement = pos=(0,0,0) rot=(0.57735,0.57735,0.57735;2.0944rad)
  sketch-geometry (4):
    g0: LineSegment StartX=176.5 StartY=18 StartZ=0 EndX=176.5 EndY=11 EndZ=0
    g1: LineSegment StartX=176.5 StartY=11 StartZ=0 EndX=183 EndY=11 EndZ=0
    g2: LineSegment StartX=183 StartY=11 StartZ=0 EndX=183 EndY=18 EndZ=0
    g3: LineSegment StartX=183 StartY=18 StartZ=0 EndX=176.5 EndY=18 EndZ=0
  constraints (12):
    c: Coincident(g0,g1)
    c: Coincident(g1,g2)
    c: Coincident(g2,g3)
    c: Coincident(g3,g0)
    c: Vertical(g0)
    c: Vertical(g2)
    c: Horizontal(g1)
    c: Horizontal(g3)
    c: PointOnObject(g0,g-3)
    c: DistanceY(g0,g0) = 7
    c: Distance(g-4,g2) = 6
    c: Distance(g3,g3) = 6.5
FEATURE [PartDesign::Pocket] Pocket001
  BaseFeature = -> Pocket
  Direction = (-1,0,0)
  Length = 505
  Length2 = 505
  Profile = -> Sketch003
  ReferenceAxis = -> Sketch003 [N_Axis]
  Suppressed = false
  Type = 4
FEATURE [PartDesign::Body] Body
  AllowCompound = false
  Group = -> [Sketch,Pad,Sketch001,Pocket,Sketch003,Pocket001]
  Origin = -> Origin
  Tip = -> Pocket001
---- part 75_drawer_box_stabilizer.FCStd = doc fcstd_503ebece76c6 ----
FCSTD DOCUMENT  (FreeCAD 1.0R39109 (Git))
Label: 75_drawer_box_stabilizer
License: All rights reserved
LicenseURL: http://en.wikipedia.org/wiki/All_rights_reserved
objects: Sketcher::SketchObject×2, Spreadsheet::Sheet×1, PartDesign::Pad×1, PartDesign::Pocket×1, PartDesign::Body×1
note: 11 computed .brp shape members not serialized (recipe doc carries the construction recipe); baked Part::Feature solids carry a one-line shape summary decoded from their .brp

FEATURE [Spreadsheet::Sheet] Spreadsheet
  cells = A2='length; B2(length)=489; A3='width; B3(width)=101; A4='height; B4(height)=18
FEATURE [Sketcher::SketchObject] Sketch
  ArcFitTolerance = 0
  AttachmentSupport = -> [XY_Plane]
  FullyConstrained = true
  MakeInternals = false
  MapMode = 5
  expr: Constraints[11] = Spreadsheet.length
  expr: Constraints[12] = Spreadsheet.width
  sketch-geometry (5):
    g0: LineSegment StartX=-244.5 StartY=50.5 StartZ=0 EndX=244.5 EndY=50.5 EndZ=0
    g1: LineSegment StartX=244.5 StartY=50.5 StartZ=0 EndX=244.5 EndY=-50.5 EndZ=0
    g2: LineSegment StartX=244.5 StartY=-50.5 StartZ=0 EndX=-244.5 EndY=-50.5 EndZ=0
    g3: LineSegment StartX=-244.5 StartY=-50.5 StartZ=0 EndX=-244.5 EndY=50.5 EndZ=0
    g4: LineSegment [constr] StartX=-244.5 StartY=50.5 StartZ=0 EndX=244.5 EndY=-50.5 EndZ=0
  constraints (13):
    c: Coincident(g0,g1)
    c: Coincident(g1,g2)
    c: Coincident(g2,g3)
    c: Coincident(g3,g0)
    c: Horizontal(g0)
    c: Horizontal(g2)
    c: Vertical(g1)
    c: Vertical(g3)
    c: Coincident(g4,g1)
    c: Coincident(g0,g4)
    c: Symmetric(g0,g1,g-1)
    c: Distance(g0,g0) = 489
    c: Distance(g0,g2) = 101
FEATURE [PartDesign::Pad] Pad
  Direction = (0,0,1)
  Length = 18
  Length2 = 10
  Profile = -> Sketch
  ReferenceAxis = -> Sketch [N_Axis]
  Suppressed = false
  Type = 0
  expr: Length = Spreadsheet.height
FEATURE [Sketcher::SketchObject] Sketch001
  ArcFitTolerance = 1e-06
  AttachmentSupport = -> [YZ_Plane]
  ExternalGeometry = -> [Pad]
  FullyConstrained = true
  MakeInternals = false
  MapMode = 5
  Placement = pos=(0,0,0) rot=(0.57735,0.57735,0.57735;2.0944rad)
  sketch-geometry (8):
    g0: LineSegment StartX=50.5 StartY=6 StartZ=0 EndX=50.5 EndY=12.5 EndZ=0
    g1: LineSegment StartX=50.5 StartY=12.5 StartZ=0 EndX=43.5 EndY=12.5 EndZ=0
    g2: LineSegment StartX=43.5 StartY=12.5 StartZ=0 EndX=43.5 EndY=6 EndZ=0
    g3: LineSegment StartX=43.5 StartY=6 StartZ=0 EndX=50.5 EndY=6 EndZ=0
    g4: LineSegment StartX=-50.5 StartY=12.5 StartZ=0 EndX=-50.5 EndY=6 EndZ=0
    g5: LineSegment StartX=-50.5 StartY=6 StartZ=0 EndX=-43.5 EndY=6 EndZ=0
    g6: LineSegment StartX=-43.5 StartY=6 StartZ=0 EndX=-43.5 EndY=12.5 EndZ=0
    g7: LineSegment StartX=-43.5 StartY=12.5 StartZ=0 EndX=-50.5 EndY=12.5 EndZ=0
  constraints (24):
    c: Coincident(g0,g1)
    c: Coincident(g1,g2)
    c: Coincident(g2,g3)
    c: Coincident(g3,g0)
    c: Vertical(g0)
    c: Vertical(g2)
    c: Horizontal(g1)
    c: Horizontal(g3)
    c: PointOnObject(g0,g-5)
    c: Coincident(g4,g5)
    c: Coincident(g5,g6)
    c: Coincident(g6,g7)
    c: Coincident(g7,g4)
    c: Vertical(g4)
    c: Vertical(g6)
    c: Horizontal(g5)
    c: Horizontal(g7)
    c: PointOnObject(g4,g-3)
    c: DistanceX(g7,g7) = 7
    c: DistanceY(g6,g6) = 6.5
    c: Distance(g-6,g5) = 6
    c: Distance(g-6,g3) = 6
    c: Equal(g7,g1)
    c: Equal(g6,g2)
FEATURE [PartDesign::Pocket] Pocket
  BaseFeature = -> Pad
  Direction = (-1,0,0)
  Length = 550
  Length2 = 555
  Profile = -> Sketch001
  ReferenceAxis = -> Sketch001 [N_Axis]
  Suppressed = false
  Type = 4
FEATURE [PartDesign::Body] Body
  AllowCompound = false
  Group = -> [Sketch,Pad,Sketch001,Pocket]
  Origin = -> Origin
  Tip = -> Pocket
